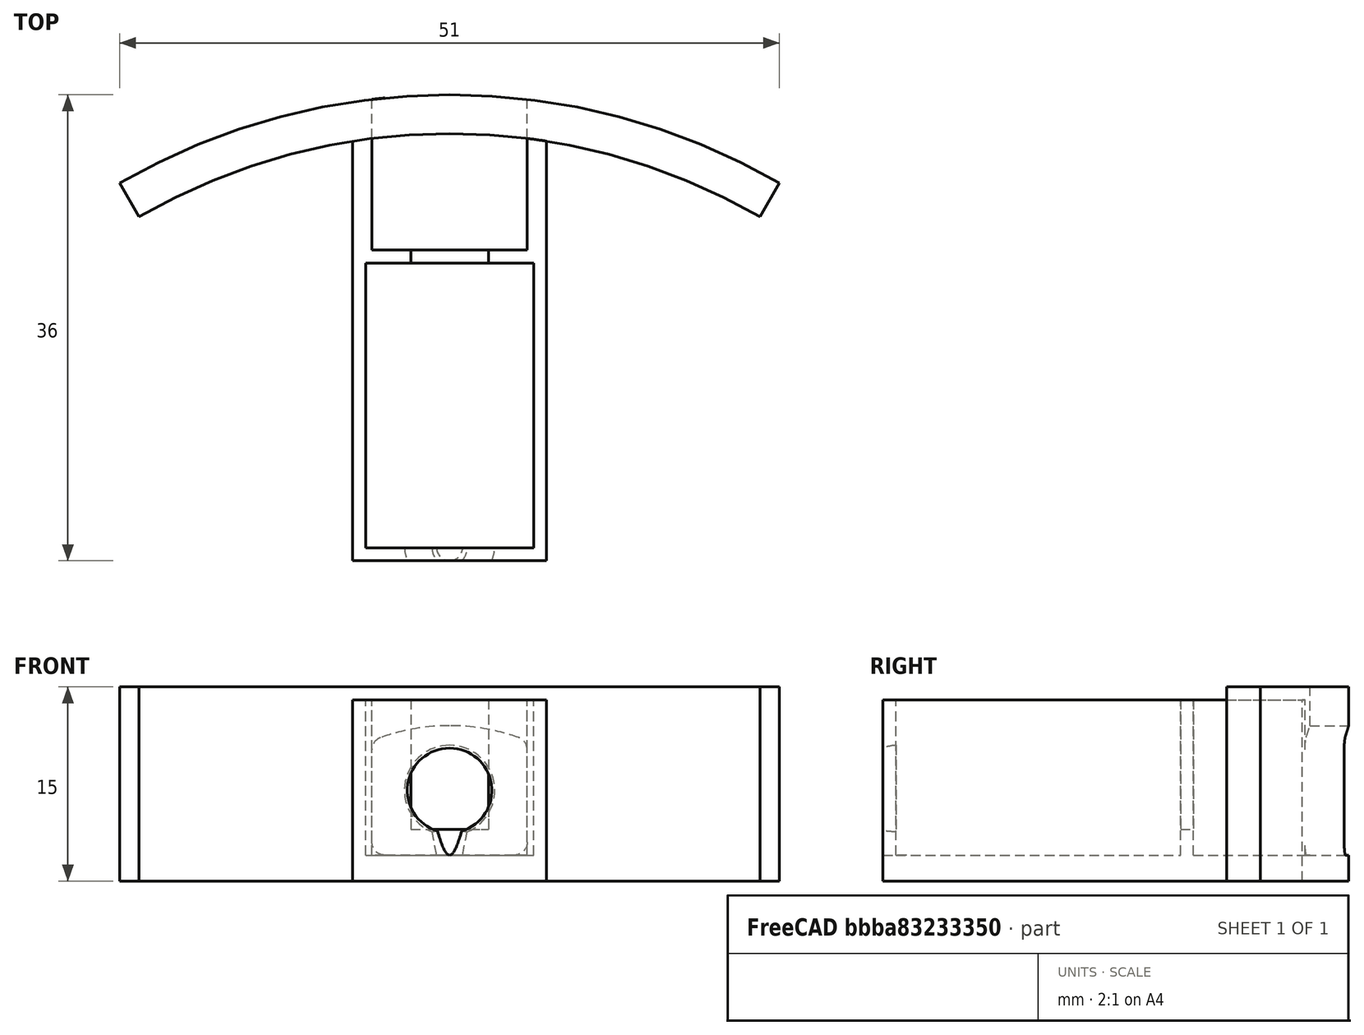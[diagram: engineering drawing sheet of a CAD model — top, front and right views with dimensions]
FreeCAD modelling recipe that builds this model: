
FCSTD DOCUMENT  (FreeCAD 0.16R4924 (Git))
Label: interior_servo_bay_v3
License: All rights reserved
LicenseURL: http://en.wikipedia.org/wiki/All_rights_reserved
objects: Part::Cut×8, Part::Box×2, Part::Cylinder×2, Part::MultiFuse×2, Part::Feature×2, Part::Extrusion×2, Part::Thickness×1
note: 19 computed .brp shape members not serialized (recipe doc carries the construction recipe); baked Part::Feature solids carry a one-line shape summary decoded from their .brp

FEATURE [Part::Box] Box  label="Case"
  Height = 14
  Length = 15
  Placement = pos=(1,6,0) rot=(0,0,1;0rad)
  Width = 34
FEATURE [Part::Cut] Cut
  Base = -> Box
FEATURE [Part::Box] Box002  label="pullBay"
  Height = 15
  Length = 12
  Placement = pos=(2.5,30,2) rot=(0,0,1;0rad)
  Width = 10
FEATURE [Part::Cut] Cut001
  Base = -> Cut
  Tool = -> Box002
FEATURE [Part::Cut] Cut002
  Base = -> Cut001
FEATURE [Part::Cut] Cut003
  Base = -> Cut002
FEATURE [Part::Cut] Cut004
  Base = -> Cut003
FEATURE [Part::Cylinder] Cylinder  label="bottle_wall"
  Angle = 60
  Height = 15
  Placement = pos=(8.5,-7,0) rot=(0,0,1;1.0472rad)
  Radius = 51
FEATURE [Part::Cylinder] Cylinder001  label="bottle_wall001"
  Angle = 60
  Height = 15
  Placement = pos=(8.5,-7,0) rot=(0,0,1;1.0472rad)
  Radius = 48
FEATURE [Part::Cut] Cut005  label="bottle_wall_composite"
  Base = -> Cylinder
  Placement = pos=(0,-2,0) rot=(0,0,1;0rad)
  Tool = -> Cylinder001
FEATURE [Part::MultiFuse] Fusion
  Shapes = -> [Cut004,Cut005]
FEATURE [Part::Cut] Cut006
  Base = -> Fusion
FEATURE [Part::Feature] Common_cs  label="pin_cs"
  Placement = pos=(3.5,35,2) rot=(0,0,1;0rad)
  shape: bbox 10 x 2e-07 x 8 mm, 0 faces, 0 solids (baked)
FEATURE [Part::Extrusion] Extrude
  Base = -> Common_cs
  Dir = (0,5,0)
  Solid = true
FEATURE [Part::Thickness] Thickness
  Faces = -> Extrude [Face7]
  Intersection = false
  Join = 0
  Mode = 0
  SelfIntersection = false
  Value = 1
FEATURE [Part::Feature] Common_cs001  label="pin_cs001"
  Placement = pos=(3.5,35,2) rot=(0,0,1;0rad)
  shape: bbox 10 x 2e-07 x 8 mm, 0 faces, 0 solids (baked)
FEATURE [Part::Extrusion] Extrude001
  Base = -> Common_cs001
  Dir = (0,5,0)
  Solid = true
FEATURE [Part::MultiFuse] Fusion001  label="bolt_bottle_side_opening"
  Placement = pos=(0,-7,1) rot=(0,0,1;0rad)
  Shapes = -> [Thickness,Extrude,Extrude001]
FEATURE [Part::Cut] Cut007
  Base = -> Cut006
  Tool = -> Fusion001
